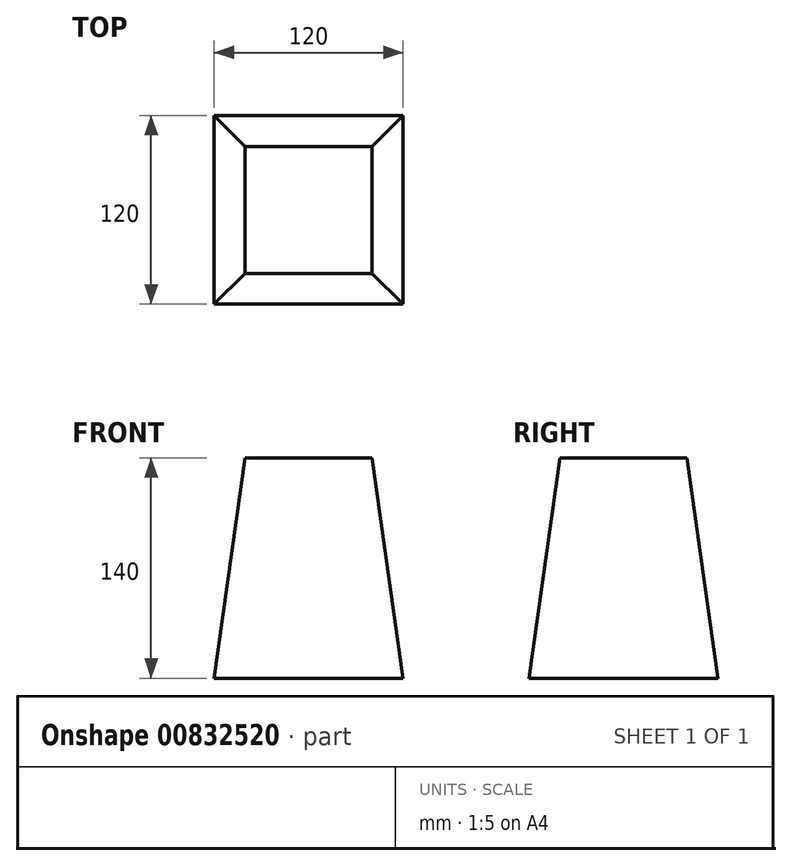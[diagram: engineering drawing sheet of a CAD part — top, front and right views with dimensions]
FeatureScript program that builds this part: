
annotation { "Feature Type Name" : "Feature", "Feature Type Description" : "" }
export const myFeature = defineFeature(function(context is Context, id is Id, definition is map)
    precondition{}
    {
        {
            var Q0;
            Q0=qCreatedBy(makeId("Top.planeOp"),FACE);
            var sketch = newSketch(context, id + "F0", { "sketchPlane" : qUnion([Q0])});
            skLineSegment(sketch, "E0.bottom", {"start": v(0, 0) * mm, "end": v(120, 0) * mm});
            skLineSegment(sketch, "E0.top", {"start": v(0, 120) * mm, "end": v(120, 120) * mm});
            skLineSegment(sketch, "E0.left", {"start": v(0, 0) * mm, "end": v(0, 120) * mm});
            skLineSegment(sketch, "E0.right", {"start": v(120, 0) * mm, "end": v(120, 120) * mm});
            skSolve(sketch);
        }
        {
            var Q0;
            Q0=makeQuery(id+"F0.imprint","IMPRINT",FACE,{"disambiguationData":[TD([[makeQuery(id+"F0.imprint","IMPRINT",EDGE,{"derivedFrom":sQuery(id+"F0.wireOp",EDGE,"E0.bottom")}),1.0]])]});
            extrude(context, id + "F1", {"entities" : qUnion([Q0]), "depth" : 140 * mm, "offsetDistance" : 25 * mm, "hasDraft" : true, "draftAngle" : 8 * degree, "draftPullDirection" : true});
        }
    });
